# Revit family: NBS_BilcoUKLtd_RfHtchs_RoofAccessHatchTypeCS-50TB
name_source: partatom
category: Doors
revit_build: Autodesk Revit 2015 (Build: 20140606_1530(x64)
units: mm (PartAtom-declared; Revit-internal decimal feet)

## types (1)
- RoofAccessHatchTypeCS-50TB
    Accessories = Many accessories available
    AcousticRating = 25 dB
    AirPermeability = 4.83 m³/hour/m² (at 600 Pa)
    AssetType = Fixed
    BIMObjectName = NBS_BilcoUKLtd_RoofHatches_RoofAccessHatchTypeCS-50TB
    Category = Pr_30_59_36_74:Roof hatches
    Color = mill finish or RAL
    Description = Aluminium thermally broken  companionway (ship stair) access hatch
    DoorLoadCapacity = ˃195 kg/m²
    DoorMaterial = 2.3 mm thick aluminium with a 127 mm beaded flange and 75 mm thick polyisocyanurate insulation
    DoorOrientation = horizontal or pitched
    DoorPosition = Raised on upstand
    DurationUnit = year
    EnvironmentalProductDeclaration = ISO 14001
    Features = Thermally broken cover and frame, engineered with compression spring operators, overlapping cover design, fully welded corners on cover and curb, constructed with corrosion resistant materials, heavy gauge construction, curb features the Bil-Clip® flashing system
    Finish = mill finish or  PPC optional
    FinishOptions = Mill finish aluminium (standard), Polyester powder coated (BS and RAL colours available)
    FireExit = Yes
    Format = External
    FrameSeal = Yes
    GlazingAreaFraction = 0
    HandicapAccessible = No
    Hardware = Heavy pintle hinges, automatic hold open arm
    HardwareFinish = NBS_Concept
    HasDrive = No
    Height = 405 mm  [stored 1.32874 ft]
    IfcExportAs = IfcDoor
    IfcExportType = NOTDEFINED
    ImpactResistance = Pass
    Infiltration = 0
    InternalSize = 1500 x 760 mm (l x w)
    IsExternal = Yes
    Kurb = 305 mm high, manufactured from 2.3 mm thick aluminium with 75 mm thick polyisocyanurate insulation
    KurbFlange = 140 mm wide with 11 mm holes
    KurbLinerOptions = No liner, Aluminium curb liner, Aluminium flanged apron design, Aluminium fully enclosed curb, Built-in louvres
    Length = 1780 mm  [stored 5.8399 ft]
    LiftingMechanismHeight = 323 mm  [stored 1.05971 ft]
    LockingOptions = Detention locks, Interior and exterior padlock hasps (standard), Keyed cylinder locks
    ManufacturerName = Bilco UK Ltd
    ManufacturerURL = www.bilcouk.com
    Material = Aluminium
    ModelNumber = CS-50TB
    ModelReference = Roof Access Hatch Type CS-50TB
    NBSCertification = www.nationalbimlibrary.com/cert/fbat0vhy
    NBSDescription = Roof hatches
    NBSReference = 45-25-28/422
    Name = RoofHatches_RoofAccessHatchTypeCS-50TB_BilcoUKLtd
    NominalHeight = 390 mm  [stored 1.27953 ft]
    NominalLength = 1780 mm  [stored 5.8399 ft]
    NominalWidth = 1040 mm  [stored 3.41207 ft]
    OperatingMechanism = Compression spring operators enclosed in telescopic tubes (manual)
    OperationControl = manual/motorised
    OperationModeOptions = Manual with interior and exterior turn handles (standard), Manual with panic latch, Motorized
    PanelLength = 1690 mm
    PanelMaterial = NBS_Concept
    PanelWidth = 950 mm  [stored 3.1168 ft]
    ProductInformation = www.bilcouk.com
    Rough Height = 0 mm  [stored 0 ft]
    Rough Width = 0 mm  [stored 0 ft]
    SecurityRating = BS EN 1627-1630
    SelfClosing = No
    Shape = Rectangular
    Size = 1780 x 1040 mm
    SmokeStop = No
    SnowLoadResistance = 1200 Pa (for 1 hour)
    StructuralOpeningLength = 1500 mm  [stored 4.92126 ft]
    StructuralOpeningWidth = 760 mm  [stored 2.49344 ft]
    ThermalTransmittance = 0.278
    Thickness = 0 mm  [stored 0 ft]
    ThirdPartyAccreditation = National Physical Laboratory and Vinci Technology Centre
    Uniclass2015Code = Pr_30_59_36_74
    Uniclass2015Title = Roof hatches
    Uniclass2015Version = Products v1.4
    UpstandHeight = 305 mm  [stored 1.00066 ft]
    UpstandMaterial = NBS_Concept
    Version = 2
    WarrantyDescription = 10 years manufacturers warranty
    WarrantyDurationParts = 10
    WarrantyDurationUnit = year
    WaterTightness = Class 9A
    Weight = With curb liner: 89 kg; Without curb liner: 81 kg
    Width = 1040 mm  [stored 3.41207 ft]
    WindResistanceClass = Class E2400
    WindSpeedResistance = 30 m/s (with open cover)

note: [stored X ft] marks values corroborated as IEEE doubles in the binary element streams (Revit-internal decimal feet)

## geometry (parser evidence)
native form markers: Sweep x10
no freeform markers — native parametric forms only
